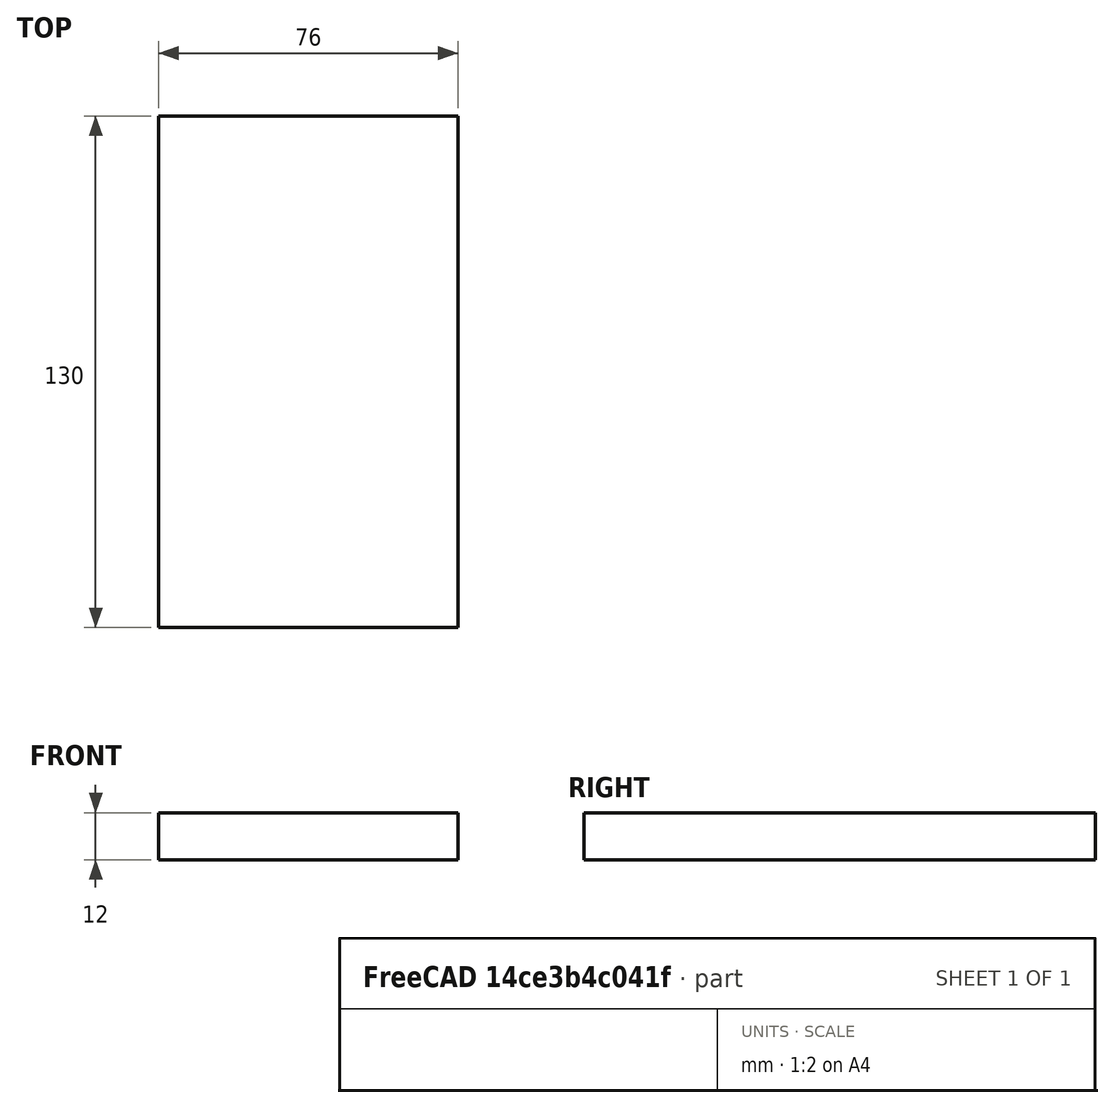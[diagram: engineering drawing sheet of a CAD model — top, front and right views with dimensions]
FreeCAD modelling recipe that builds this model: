
FCSTD DOCUMENT  (FreeCAD 0.16R6703 (Git))
Label: box2_inside
License: All rights reserved
LicenseURL: http://en.wikipedia.org/wiki/All_rights_reserved
objects: Drawing::FeatureViewPython×3, Drawing::FeatureViewPart×2, Sketcher::SketchObject×1, PartDesign::Pad×1, Drawing::FeaturePage×1
note: 3 computed .brp shape members not serialized (recipe doc carries the construction recipe); baked Part::Feature solids carry a one-line shape summary decoded from their .brp

FEATURE [Sketcher::SketchObject] Sketch
  expr: Constraints[9] = 100 - 2 * 12
  sketch-geometry (4):
    g0: LineSegment StartX=0 StartY=0 StartZ=0 EndX=76 EndY=0 EndZ=0
    g1: LineSegment StartX=76 StartY=0 StartZ=0 EndX=76 EndY=130 EndZ=0
    g2: LineSegment StartX=76 StartY=130 StartZ=0 EndX=0 EndY=130 EndZ=0
    g3: LineSegment StartX=0 StartY=130 StartZ=0 EndX=0 EndY=0 EndZ=0
  constraints (11):
    c: Coincident(g0,g1)
    c: Coincident(g1,g2)
    c: Coincident(g2,g3)
    c: Coincident(g3,g0)
    c: Horizontal(g0)
    c: Horizontal(g2)
    c: Vertical(g1)
    c: Vertical(g3)
    c: Coincident(g0,g-1)
    c: Distance(g0) = 76
    c: Distance(g3) = 130
FEATURE [PartDesign::Pad] Pad
  Length = 12
  Length2 = 100
  Sketch = -> Sketch
  Type = 0
FEATURE [Drawing::FeatureViewPart] Ortho  label="Ortho_0_0"
  Direction = (1,0,0)
  HiddenWidth = 0.15
  LineWidth = 0.35
  Rotation = -90
  Scale = 1.5
  ShowHiddenLines = false
  ShowSmoothLines = false
  Source = -> Pad
  Tolerance = 0.05
  ViewResult = <g id="Ortho_0_0"\n   transform="rotate(-90,112.5,56.3333) translate(112.5,56.3333) scale(1.5,1.5)"\n  >\n<g   stroke="rgb(0, 0, 0)"\n   stroke-width="0.233333"\n   stroke-linecap="butt"\n   stroke-linejoin="miter"\n   fill="none"\n   transform="scale(1,-1)"\n  >\n<path id= "1" d=" M 0 0 L 12 0 " />\n<path id= "2" d=" M 0 -130 L 12 -130 " />\n<path id= "3" d=" M 0 0 L 0 -130 " />\n<path id= "4" d=" M 12 0 L 12 -130 " />\n</g>\n</g>
  Visible = true
  X = 112.5
  Y = 56.3333
FEATURE [Drawing::FeatureViewPart] Ortho001  label="Ortho_0_-1"
  Direction = (0,0,-1)
  HiddenWidth = 0.15
  LineWidth = 0.35
  Rotation = 90
  Scale = 1.5
  ShowHiddenLines = false
  ShowSmoothLines = false
  Source = -> Pad
  Tolerance = 0.05
  ViewResult = <g id="Ortho_0_-1"\n   transform="rotate(90,112.5,198.667) translate(112.5,198.667) scale(1.5,1.5)"\n  >\n<g   stroke="rgb(0, 0, 0)"\n   stroke-width="0.233333"\n   stroke-linecap="butt"\n   stroke-linejoin="miter"\n   fill="none"\n   transform="scale(1,-1)"\n  >\n<path id= "1" d=" M 0 0 L -76 0 " />\n<path id= "2" d=" M -76 0 L -76 130 " />\n<path id= "3" d=" M -76 130 L 0 130 " />\n<path id= "4" d=" M 0 130 L 0 0 " />\n</g>\n</g>
  Visible = true
  X = 112.5
  Y = 198.667
FEATURE [Drawing::FeatureViewPython] dim001  # drawing view (typed FeaturePython)
  Rotation = 0
  ViewResult = <g> \n  <line x1="110.500000" y1="198.667000" x2="92.857833" y2="198.667000" style="stroke:rgb(0,0,255);stroke-width:0.50" />\n<line x1="110.500000" y1="84.667000" x2="92.857833" y2="84.667000" style="stroke:rgb(0,0,255);stroke-width:0.50" />\n<line x1="93.857833" y1="198.667000" x2="93.857833" y2="84.667000" style="stroke:rgb(0,0,255);stroke-width:0.50" /> \n  <polygon points="93.857833,84.667000 92.857833,87.667000 93.857833,88.667000 94.857833,87.667000" style="fill:rgb(0,0,255);stroke:rgb(0,0,255);stroke-width:0" /><polygon points="93.857833,198.667000 94.857833,195.667000 93.857833,194.667000 92.857833,195.667000" style="fill:rgb(0,0,255);stroke:rgb(0,0,255);stroke-width:0" /> \n  <text x="91.857833" y="141.667000" font-family="inherit" font-size="7" fill="rgb(0,0,255)" text-anchor="middle" transform="rotate(-90.000000 91.857833,141.667000)" >76</text> </g>
  Visible = true
  X = 0
  Y = 0
  arrowL1 = 3
  arrowL2 = 1
  arrowW = 2
  arrow_scheme = 0
  autoPlaceOffset = 2
  autoPlaceText = true
  click1_x = 93.8578
  click1_y = 101.679
  click2_x = 93.8578
  click2_y = 101.679
  comma_decimal_place = false
  dimension_line_overshoot = 1
  gap_datum_points = 2
  halfDimension_linear = false
  lineColor = rgb(0,0,255)
  strokeWidth = 0.5
  textFormat_linear = %(value)3.3f
  textRenderer_color = rgb(0,0,255)
  textRenderer_family = inherit
  textRenderer_size = 7
  unit_custom_scale = 0.8
  unit_scheme = 0
FEATURE [Drawing::FeatureViewPython] dim002  # drawing view (typed FeaturePython)
  Rotation = 0
  ViewResult = <g> \n  <line x1="307.500000" y1="200.667000" x2="307.500000" y2="213.246691" style="stroke:rgb(0,0,255);stroke-width:0.50" />\n<line x1="112.500000" y1="200.667000" x2="112.500000" y2="213.246691" style="stroke:rgb(0,0,255);stroke-width:0.50" />\n<line x1="307.500000" y1="212.246691" x2="112.500000" y2="212.246691" style="stroke:rgb(0,0,255);stroke-width:0.50" /> \n  <polygon points="112.500000,212.246691 115.500000,213.246691 116.500000,212.246691 115.500000,211.246691" style="fill:rgb(0,0,255);stroke:rgb(0,0,255);stroke-width:0" /><polygon points="307.500000,212.246691 304.500000,211.246691 303.500000,212.246691 304.500000,213.246691" style="fill:rgb(0,0,255);stroke:rgb(0,0,255);stroke-width:0" /> \n  <text x="210.000000" y="210.246691" font-family="inherit" font-size="7" fill="rgb(0,0,255)" text-anchor="middle" transform="rotate(0.000000 210.000000,210.246691)" >130</text> </g>
  Visible = true
  X = 0
  Y = 0
  arrowL1 = 3
  arrowL2 = 1
  arrowW = 2
  arrow_scheme = 0
  autoPlaceOffset = 2
  autoPlaceText = true
  click1_x = 156.074
  click1_y = 212.247
  click2_x = 156.074
  click2_y = 212.247
  comma_decimal_place = false
  dimension_line_overshoot = 1
  gap_datum_points = 2
  halfDimension_linear = false
  lineColor = rgb(0,0,255)
  strokeWidth = 0.5
  textFormat_linear = %(value)3.3f
  textRenderer_color = rgb(0,0,255)
  textRenderer_family = inherit
  textRenderer_size = 7
  unit_custom_scale = 0.8
  unit_scheme = 0
FEATURE [Drawing::FeatureViewPython] dim003  # drawing view (typed FeaturePython)
  Rotation = 0
  ViewResult = <g> \n  <line x1="110.500000" y1="56.333300" x2="93.213355" y2="56.333300" style="stroke:rgb(0,0,255);stroke-width:0.50" />\n<line x1="110.500000" y1="38.333300" x2="93.213355" y2="38.333300" style="stroke:rgb(0,0,255);stroke-width:0.50" />\n<line x1="94.213355" y1="56.333300" x2="94.213355" y2="38.333300" style="stroke:rgb(0,0,255);stroke-width:0.50" /> \n  <polygon points="94.213355,38.333300 93.213355,41.333300 94.213355,42.333300 95.213355,41.333300" style="fill:rgb(0,0,255);stroke:rgb(0,0,255);stroke-width:0" /><polygon points="94.213355,56.333300 95.213355,53.333300 94.213355,52.333300 93.213355,53.333300" style="fill:rgb(0,0,255);stroke:rgb(0,0,255);stroke-width:0" /> \n  <text x="92.213355" y="47.333300" font-family="inherit" font-size="7" fill="rgb(0,0,255)" text-anchor="middle" transform="rotate(-90.000000 92.213355,47.333300)" >12</text> </g>
  Visible = true
  X = 0
  Y = 0
  arrowL1 = 3
  arrowL2 = 1
  arrowW = 2
  arrow_scheme = 0
  autoPlaceOffset = 2
  autoPlaceText = true
  click1_x = 94.2134
  click1_y = 49.062
  click2_x = 94.2134
  click2_y = 49.062
  comma_decimal_place = false
  dimension_line_overshoot = 1
  gap_datum_points = 2
  halfDimension_linear = false
  lineColor = rgb(0,0,255)
  strokeWidth = 0.5
  textFormat_linear = %(value)3.3f
  textRenderer_color = rgb(0,0,255)
  textRenderer_family = inherit
  textRenderer_size = 7
  unit_custom_scale = 0.8
  unit_scheme = 0
FEATURE [Drawing::FeaturePage] Page
  EditableTexts = AUTHOR NAME | CREATION DATE | SUPERVISOR NAME | CHECK DATE | SCALE | WEIGHT | NUMBER | SHEET | box2 inside | SUBTITLE
  Group = -> [Ortho,Ortho001,dim001,dim002,dim003]
